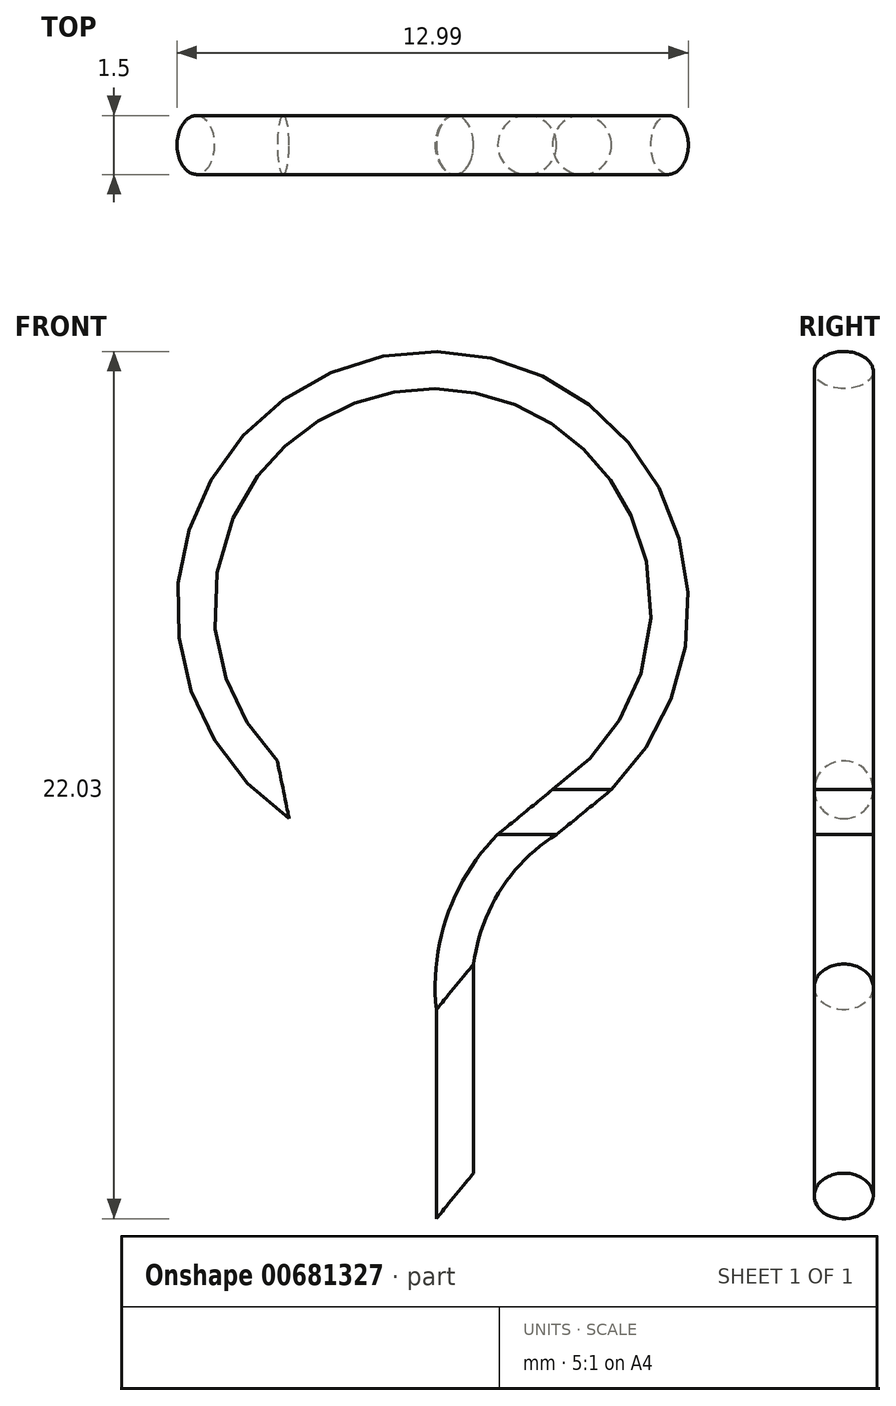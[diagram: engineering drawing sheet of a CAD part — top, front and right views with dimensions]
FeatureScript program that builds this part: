
annotation { "Feature Type Name" : "Feature", "Feature Type Description" : "" }
export const myFeature = defineFeature(function(context is Context, id is Id, definition is map)
    precondition{}
    {
        {
            var Q0;
            Q0=qCreatedBy(makeId("Front.planeOp"),FACE);
            var sketch = newSketch(context, id + "F0", { "sketchPlane" : qUnion([Q0])});
            skArc(sketch, "E0", {"start": v(0, 0) * mm, "mid": v(-3.8, 10.63) * mm, "end": v(-7.59, 0) * mm});
            skLineSegment(sketch, "E1", {"start": v(0, 0) * mm, "end": v(-1.4, -1.14) * mm});
            skLineSegment(sketch, "E2", {"start": v(-3.23, -5.01) * mm, "end": v(-3.23, -10.32) * mm});
            skPoint(sketch, "E3.visualSharp", {"position": v(-3.23, -2.64) * mm});
            skArc(sketch, "E3.filletArc", {"start": v(-1.4, -1.14) * mm, "mid": v(-2.75, -2.87) * mm, "end": v(-3.23, -5.01) * mm});
            skSolve(sketch);
        }
        {
            var Q0;
            Q0=qCreatedBy(makeId("Top.planeOp"),FACE);
            var sketch = newSketch(context, id + "F1", { "sketchPlane" : qUnion([Q0])});
            skCircle(sketch, "E4", {"center": v(0, 0) * mm, "radius": 0.75 * mm});
            skSolve(sketch);
        }
        {
            var Q0;
            Q0=makeQuery(id+"F1.imprint","IMPRINT",FACE,{"disambiguationData":[TD([[makeQuery(id+"F1.imprint","IMPRINT",EDGE,{"derivedFrom":sQuery(id+"F1.wireOp",EDGE,"E4")}),1.0]])]});
            var Q1;
            Q1=sQuery(id+"F0.wireOp",EDGE,"E0");
            var Q2;
            Q2=sQuery(id+"F0.wireOp",EDGE,"E3.filletArc");
            var Q3;
            Q3=sQuery(id+"F0.wireOp",EDGE,"E1");
            var Q4;
            Q4=sQuery(id+"F0.wireOp",EDGE,"E2");
            sweep(context, id + "F2", {"profiles" : qUnion([Q0]), "path" : qUnion([Q1, Q2, Q3, Q4])});
        }
    });
